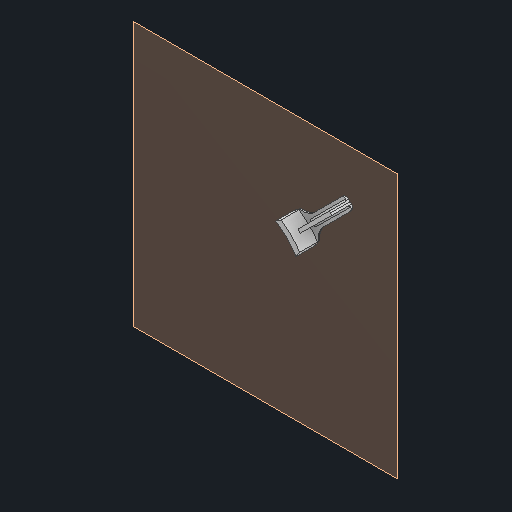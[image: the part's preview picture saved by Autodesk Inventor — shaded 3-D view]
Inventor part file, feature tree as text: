
AUTODESK INVENTOR PART (.ipt)
format: ipt  version: 2023.1 (Build 271208000, 208)  size: 195,584 bytes
history: native  units: mm
features: other x3, extrude x2, chamfer x2, sketch x2, plane x1
ambient origin geometry x8: Origin, YZ Plane, XZ Plane, XY Plane, X Axis, Y Axis, Z Axis, Center Point
bodies: Solid1 (feature_tree)
feature tree (10):
  plane  "Work Plane1"
  extrude  "Extrusion1"  Depth=147.0mm
  extrude  "Extrusion2"  Depth=2.0mm
  chamfer  "Chamfer1"  Distance=7.5mm
  chamfer  "Chamfer2"  Distance=142.0mm
  sketch  "Sketch1"  dims[d0=157.0mm d1=147.0mm]
  sketch  "Sketch2"  dims[d2=45.0deg d3=7.5mm d4=7.5mm d5=142.0mm d6=135.0deg d7=135.0deg d8=22.5mm d9=22.5mm d10=5.0mm d11=2.0mm d12=0.0mm d13=157.0mm d14=7.5mm d16=135.0deg d21=2.0mm d22=2.0mm d23=22.0mm d24=0.0mm d25=60.0mm d26=2.0mm d27=4.0mm d28=45.0deg d29=2.0mm d30=2.0mm d31=45.0deg d32=10.0mm d33=10.0mm d34=10.0mm d35=10.0mm d36=5.0mm d37=2.0mm d38=45.0deg]
  parser-record x1  (decoder bookkeeping rows leaked as tree rows — omitted from the tree; the rows remain in map.json)
  other  "Beau4tClock.iam"
  other  "Clock:1"
note: 1 file-system path scrubbed to <path> (originals preserved in map.json)
